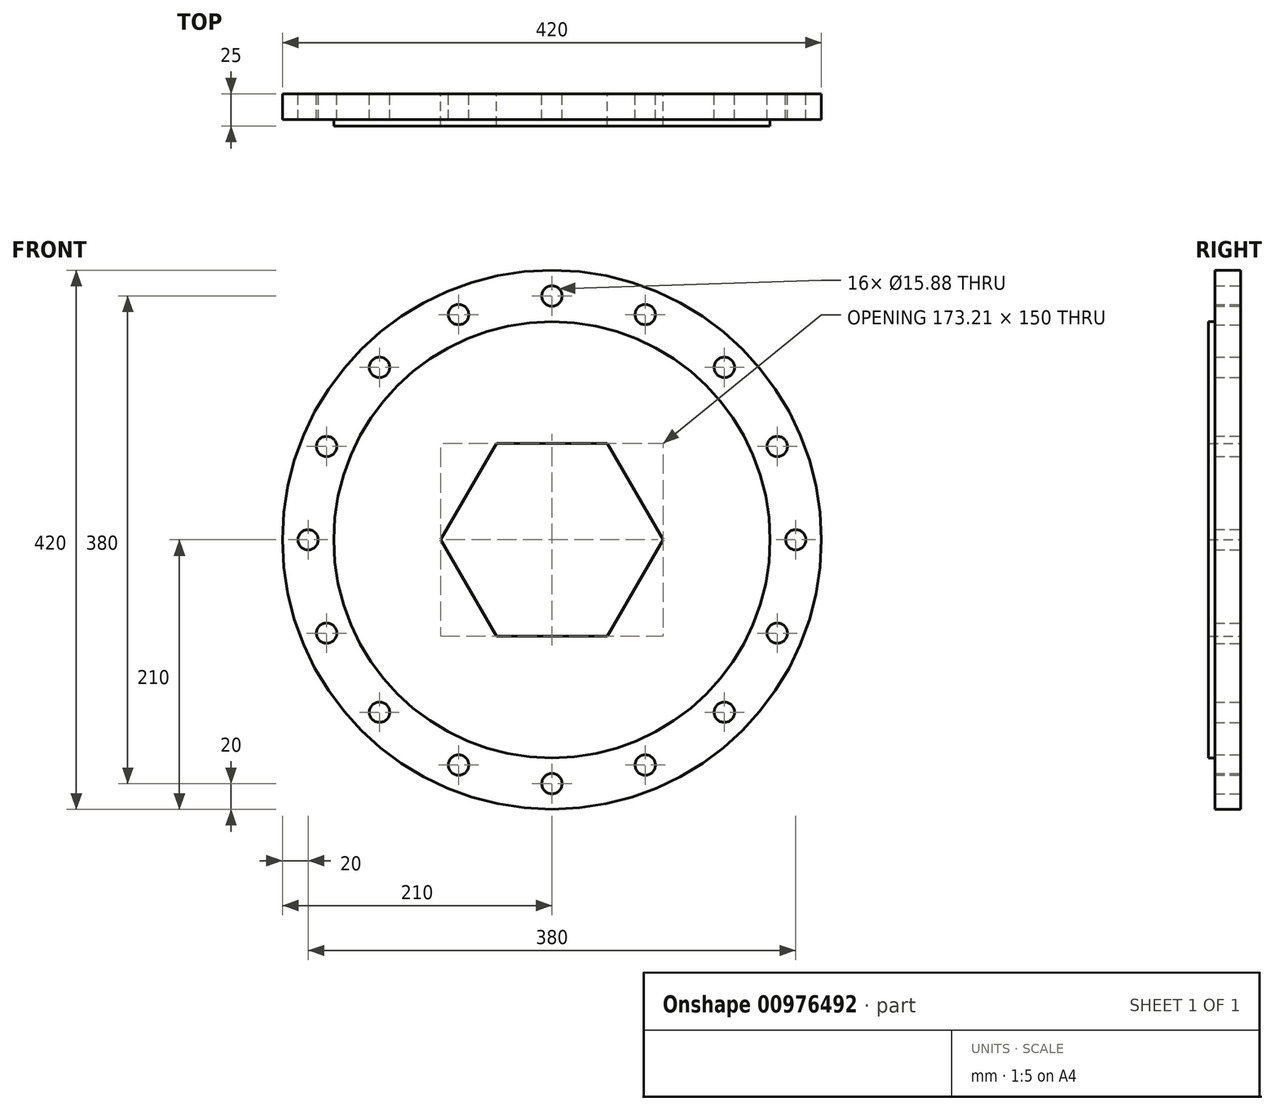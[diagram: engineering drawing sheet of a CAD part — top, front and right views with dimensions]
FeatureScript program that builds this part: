
annotation { "Feature Type Name" : "Feature", "Feature Type Description" : "" }
export const myFeature = defineFeature(function(context is Context, id is Id, definition is map)
    precondition{}
    {
        {
            var Q0;
            Q0=qCreatedBy(makeId("Front.planeOp"),FACE);
            var sketch = newSketch(context, id + "F0", { "sketchPlane" : qUnion([Q0])});
            skCircle(sketch, "E0", {"center": v(0, 0) * mm, "radius": 210 * mm});
            skLineSegment(sketch, "E1.anchor1", {"start": v(0, 0) * mm, "end": v(0, 190) * mm, "construction": true});
            skCircle(sketch, "E2", {"center": v(0, 190) * mm, "radius": 7.94 * mm});
            skCircle(sketch, "E3.1.0", {"center": v(-72.7, 175.54) * mm, "radius": 7.94 * mm});
            skCircle(sketch, "E3.2.0", {"center": v(-134.35, 134.35) * mm, "radius": 7.94 * mm});
            skCircle(sketch, "E3.3.0", {"center": v(-175.54, 72.7) * mm, "radius": 7.94 * mm});
            skCircle(sketch, "E3.4.0", {"center": v(-190, 0) * mm, "radius": 7.94 * mm});
            skCircle(sketch, "E3.5.0", {"center": v(-175.54, -72.7) * mm, "radius": 7.94 * mm});
            skCircle(sketch, "E3.6.0", {"center": v(-134.35, -134.35) * mm, "radius": 7.94 * mm});
            skCircle(sketch, "E3.7.0", {"center": v(-72.7, -175.54) * mm, "radius": 7.94 * mm});
            skCircle(sketch, "E3.8.0", {"center": v(0, -190) * mm, "radius": 7.94 * mm});
            skCircle(sketch, "E3.9.0", {"center": v(72.7, -175.54) * mm, "radius": 7.94 * mm});
            skCircle(sketch, "E3.10.0", {"center": v(134.35, -134.35) * mm, "radius": 7.94 * mm});
            skCircle(sketch, "E3.11.0", {"center": v(175.54, -72.7) * mm, "radius": 7.94 * mm});
            skCircle(sketch, "E3.12.0", {"center": v(190, 0) * mm, "radius": 7.94 * mm});
            skCircle(sketch, "E3.13.0", {"center": v(175.54, 72.7) * mm, "radius": 7.94 * mm});
            skCircle(sketch, "E3.14.0", {"center": v(134.35, 134.35) * mm, "radius": 7.94 * mm});
            skCircle(sketch, "E3.15.0", {"center": v(72.7, 175.54) * mm, "radius": 7.94 * mm});
            skCircle(sketch, "E4.cCircle", {"center": v(0, 0) * mm, "radius": 75 * mm, "construction": true});
            skLineSegment(sketch, "E4.0", {"start": v(86.6, 0) * mm, "end": v(43.3, -75) * mm});
            skLineSegment(sketch, "E4.1", {"start": v(43.3, -75) * mm, "end": v(-43.3, -75) * mm});
            skLineSegment(sketch, "E4.2", {"start": v(-43.3, -75) * mm, "end": v(-86.6, 0) * mm});
            skLineSegment(sketch, "E4.3", {"start": v(-86.6, 0) * mm, "end": v(-43.3, 75) * mm});
            skLineSegment(sketch, "E4.4", {"start": v(-43.3, 75) * mm, "end": v(43.3, 75) * mm});
            skLineSegment(sketch, "E4.5", {"start": v(43.3, 75) * mm, "end": v(86.6, 0) * mm});
            skPoint(sketch, "E4.0.midPoint", {"position": v(64.95, -37.5) * mm});
            skSolve(sketch);
        }
        {
            var Q0;
            Q0 = qSketchRegion(id + "F0", true);
            extrude(context, id + "F1", {"entities" : qUnion([Q0]), "depth" : 25 * mm, "offsetDistance" : 25 * mm});
        }
        {
            var Q0;
            Q0=makeQuery(id+"F1.opExtrude","CAP_FACE",FACE,{"disambiguationData":[OSD([sQuery(id+"F0.wireOp",EDGE,"E0"),sQuery(id+"F0.wireOp",EDGE,"E2"),sQuery(id+"F0.wireOp",EDGE,"E3.1.0"),sQuery(id+"F0.wireOp",EDGE,"E3.2.0"),sQuery(id+"F0.wireOp",EDGE,"E3.3.0"),sQuery(id+"F0.wireOp",EDGE,"E3.4.0"),sQuery(id+"F0.wireOp",EDGE,"E3.5.0"),sQuery(id+"F0.wireOp",EDGE,"E3.6.0"),sQuery(id+"F0.wireOp",EDGE,"E3.7.0"),sQuery(id+"F0.wireOp",EDGE,"E3.8.0"),sQuery(id+"F0.wireOp",EDGE,"E3.9.0"),sQuery(id+"F0.wireOp",EDGE,"E3.10.0"),sQuery(id+"F0.wireOp",EDGE,"E3.11.0"),sQuery(id+"F0.wireOp",EDGE,"E3.12.0"),sQuery(id+"F0.wireOp",EDGE,"E3.13.0"),sQuery(id+"F0.wireOp",EDGE,"E3.14.0"),sQuery(id+"F0.wireOp",EDGE,"E3.15.0"),sQuery(id+"F0.wireOp",EDGE,"E4.0"),sQuery(id+"F0.wireOp",EDGE,"E4.1"),sQuery(id+"F0.wireOp",EDGE,"E4.2"),sQuery(id+"F0.wireOp",EDGE,"E4.3"),sQuery(id+"F0.wireOp",EDGE,"E4.4"),sQuery(id+"F0.wireOp",EDGE,"E4.5")])],"isStart":false});
            var sketch = newSketch(context, id + "F2", { "sketchPlane" : qUnion([Q0])});
            skCircle(sketch, "E5", {"center": v(0, 0) * mm, "radius": 170 * mm});
            skCircle(sketch, "E6", {"center": v(0, 0) * mm, "radius": 210 * mm});
            skSolve(sketch);
        }
        {
            var Q0;
            Q0 = qSketchRegion(id + "F2", true);
            extrude(context, id + "F3", {"entities" : qUnion([Q0]), "operationType" : NewBodyOperationType.REMOVE, "oppositeDirection" : true, "depth" : 5 * mm, "offsetDistance" : 25 * mm});
        }
    });
